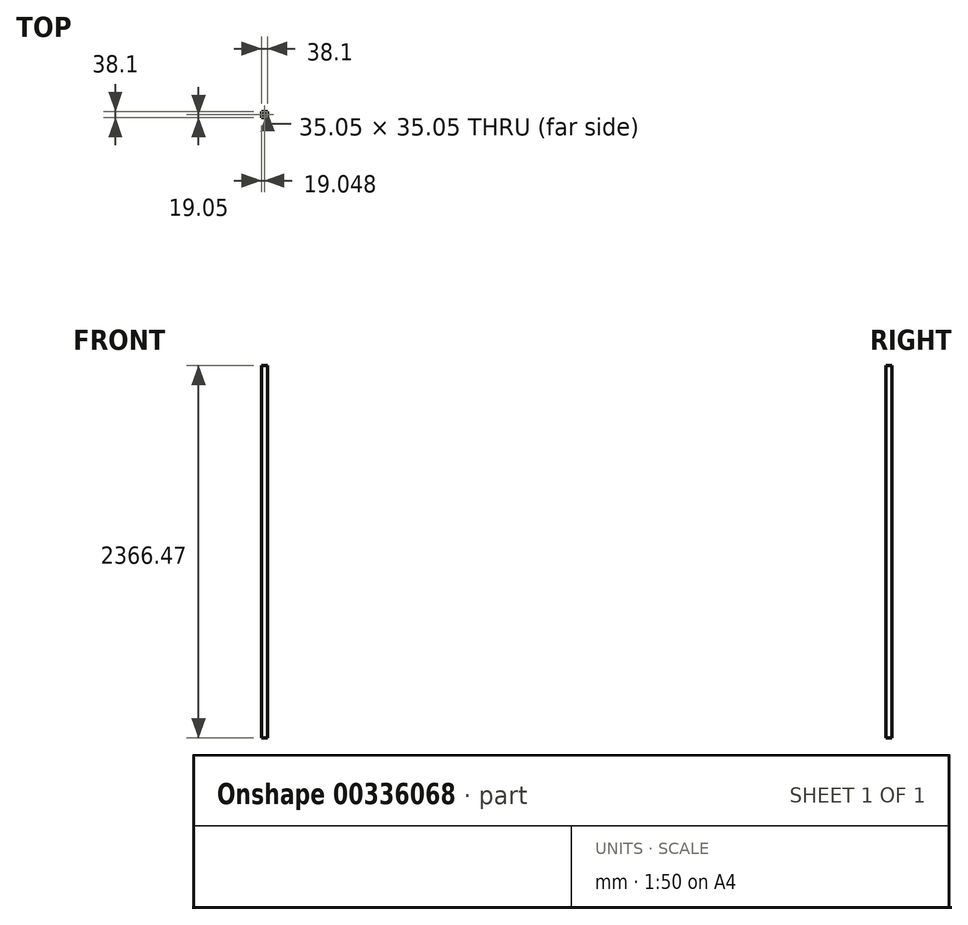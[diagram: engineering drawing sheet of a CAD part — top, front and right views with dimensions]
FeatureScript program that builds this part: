
annotation { "Feature Type Name" : "Feature", "Feature Type Description" : "" }
export const myFeature = defineFeature(function(context is Context, id is Id, definition is map)
    precondition{}
    {
        {
            var Q0;
            Q0=qCreatedBy(makeId("Front.planeOp"),FACE);
            var sketch = newSketch(context, id + "F0", { "sketchPlane" : qUnion([Q0])});
            skLineSegment(sketch, "E0.bottom", {"start": v(-146.7, 1399.42) * mm, "end": v(-108.6, 1399.42) * mm});
            skLineSegment(sketch, "E0.top", {"start": v(-146.7, -967.05) * mm, "end": v(-108.6, -967.05) * mm});
            skLineSegment(sketch, "E0.left", {"start": v(-146.7, 1399.42) * mm, "end": v(-146.7, -967.05) * mm});
            skLineSegment(sketch, "E0.right", {"start": v(-108.6, 1399.42) * mm, "end": v(-108.6, -967.05) * mm});
            skSolve(sketch);
        }
        {
            var Q0;
            Q0=qSketchRegion(id+"F0",true);
            extrude(context, id + "F1", {"entities" : qUnion([Q0]), "depth" : 38.1 * mm});
        }
        {
            var Q0;
            Q0=makeQuery(id+"F1.opExtrude","SWEPT_FACE",FACE,{"disambiguationData":[OSD([sQuery(id+"F0.wireOp",EDGE,"E0.bottom")])]});
            var sketch = newSketch(context, id + "F2", { "sketchPlane" : qUnion([Q0])});
            skLineSegment(sketch, "E1.0", {"start": v(-145.18, -1.52) * mm, "end": v(-110.13, -1.52) * mm});
            skLineSegment(sketch, "E1.1", {"start": v(-145.18, -36.58) * mm, "end": v(-145.18, -1.52) * mm});
            skLineSegment(sketch, "E1.2", {"start": v(-145.18, -36.58) * mm, "end": v(-110.13, -36.58) * mm});
            skLineSegment(sketch, "E1.3", {"start": v(-110.13, -36.58) * mm, "end": v(-110.13, -1.52) * mm});
            skSolve(sketch);
        }
        {
            var Q0;
            Q0=qSketchRegion(id+"F2",true);
            extrude(context, id + "F3", {"entities" : qUnion([Q0]), "operationType" : NewBodyOperationType.REMOVE, "oppositeDirection" : true, "depth" : 2540 * mm});
        }
    });
